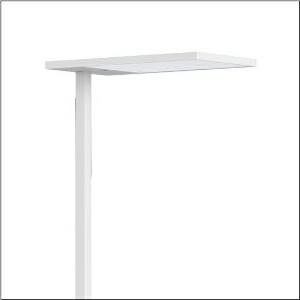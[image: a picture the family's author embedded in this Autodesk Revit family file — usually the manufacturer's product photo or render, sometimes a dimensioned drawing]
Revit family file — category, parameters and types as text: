
# Revit family: silica_r__21_floor_r_51mx53sg4dw_45fa
name_source: partatom
category: Lighting Fixtures
units: mm (PartAtom-declared; Revit-internal decimal feet)

## family parameters
Cut with Voids When Loaded = No
Host = Face
Light Source = No
Part Type = Normal
Room Calculation Point = No
Round Connector Dimension = Use Diameter
Shared = No

## types (1)
- Silica® 21 Floor R (1 x LED, 15000 lm, 106.4 W, 4000K)
    Apparent Load = 106 VA
    CIE Flux Codes = 54 86 97 13 100
    Color Rendering = 80
    Color Temperature = 4000K
    Default Elevation = 1800 mm
    Description = Silica® 21 Floor R, floorstanding luminaire, of PMMA, primary optical cover: prismatic diffuser, of PMMA, CAT 2 (L<= 3000cd/m²), light emission: indirect/direct distribution, primary light characteristic: symmetric, primary optical cover: cover panel, of PMMA, installation type: not mounted, LED, rated luminous flux: 15.000lm, luminous efficacy: 141lm/W, light colour: 840, colour temperature: 4000K, control gear: DALI 2, daylight-dependent control, mains connection: 230V, AC, 50/60Hz, connection cable pre-assembled, cable length: 2,5m, rated input power: 106.4W, luminaire head, of aluminium, coated, traffic white (RAL 9016), length: 671mm, width: 330mm, height: 2010mm, supporting column, angular, of aluminium, coated, traffic white (RAL 9016), baseplate, of steel, coated, traffic white (RAL 9016), protection rating (complete): IP20, insulation class (complete): insulation class I (protective earthing), certification: CE, standard: EN 50419, packaging unit: 1 piece
    Height = 18 mm
    Lamp = 1 x LED
    Lamp Light Flux = 15000 lm
    Lamp Power = 106.4 W
    Lamp count = 1
    Length = 650 mm
    Luminous efficacy = 141 lm/W
    Manufacturer = Siteco
    ModVariant = No
    Model = 51MX53SG4DW
    Mounting Place = Floor
    Mounting Type = Freestanding
    Number of Poles = 1
    OnlyDefault = Yes
    Power Factor = 1
    Product Name = Silica® 21 Floor R
    Product group = floorstanding luminaire
    ProductGroupID = 1302
    Protection Class = Protection class I
    Protection Degree = IP 20
    RLX_Detail_Level = 1
    RLX_Emergency_Light_Flux = 0 lm
    RLX_Emergency_Type = 0
    RLX_Emergency_Type_DB = No
    RlxData = <blob elided: 18601 chars, md5=e205cfe1>
    Socket = socket
    Standby Power = 0 W
    System Light Flux = 15000 lm
    System Power = 106 W
    Type Comments = Product without accessories
    Type Image = l_1003935.jpg
    URL = http://relux.com
    VarID = ---
    Voltage = 0 V
    Weight = 0.00 kg
    Width = 350 mm

## geometry (parser evidence)
native form markers: Blend x4, Sweep x16
no freeform markers — native parametric forms only
